# Revit family: RBM Noor 6070
name_source: partatom
category: Furniture
revit_build: Autodesk Revit Architecture 2014 (Build: 20131024_2115(x64)
units: mm (PartAtom-declared; Revit-internal decimal feet)

## types (1)
- RBM Noor 6070
    BIMobject category = Office Furniture
    Design country = Sweden
    EAN code = http://-
    Edition number = 1
    IFC Classification = Furniture
    Installation instructions = http://www.sbseating.com
    Manufacturer country = Sweden
    Manufacturer name = Scandinavian Business Seating
    Material = SBS_ RBM Noor - 6070_ Steel
    Material Main = SBS_ RBM Noor - 6070 Seat
    Material Secondary = SBS_ RBM Noor - 6070 Plastic Black
    Material main = Aluminium
    Material secondary = Plastic
    Matt Finish = SBS_ RBM Noor - 6070 Seat
    NBS Reference Code = 35-12-57
    NBS Reference Description = Office Chairs
    Product SKU = rbm_n_6070
    Product data url = http://sbs.bimobject.com
    Product family = Canteen and conference chairs
    Product group = RBM Noor
    Product name = RBM Noor 6070
    QR code = http://sbs.bimobject.com
    Technical description = http://www.sbseating.com
    UNSPSC Code = 56
    Uniclass 1.4 Code = L853
    Uniclass 1.4 Description = Office furniture
    Uniclass 2.0 Code = PR-35-12-57
    Weight Net (Kg) = 0
    Width = 536 mm

## geometry (parser evidence)
native form markers: Blend x4, Sweep x19
no freeform markers — native parametric forms only
